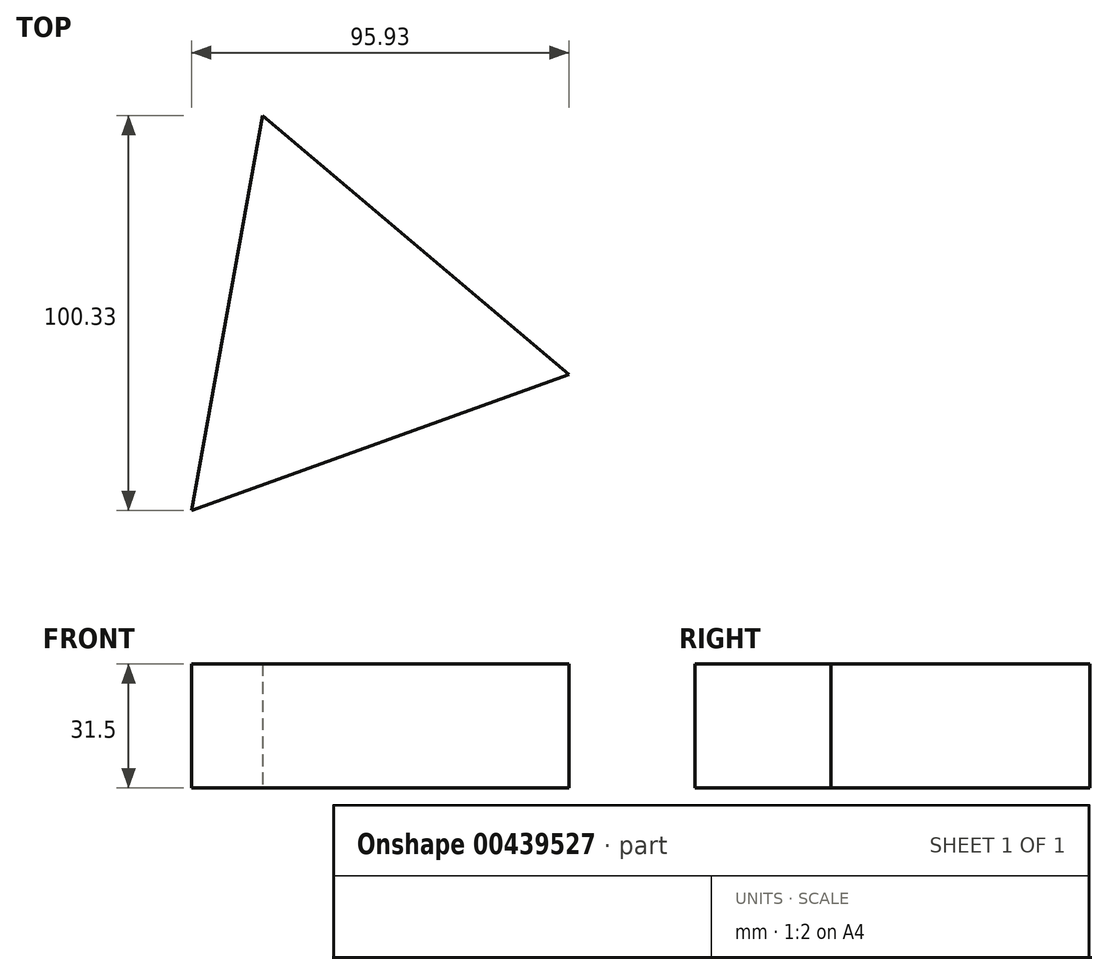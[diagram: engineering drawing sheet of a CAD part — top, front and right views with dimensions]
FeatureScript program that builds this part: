
annotation { "Feature Type Name" : "Feature", "Feature Type Description" : "" }
export const myFeature = defineFeature(function(context is Context, id is Id, definition is map)
    precondition{}
    {
        {
            var Q0;
            Q0=qCreatedBy(makeId("Top.planeOp"),FACE);
            var sketch = newSketch(context, id + "F0", { "sketchPlane" : qUnion([Q0])});
            skCircle(sketch, "E0.cCircle", {"center": v(0, 14.91) * mm, "radius": 29.43 * mm, "construction": true});
            skLineSegment(sketch, "E0.0", {"start": v(57.92, 4.46) * mm, "end": v(-38.01, -30.03) * mm});
            skLineSegment(sketch, "E0.1", {"start": v(-38.01, -30.03) * mm, "end": v(-19.91, 70.3) * mm});
            skLineSegment(sketch, "E0.2", {"start": v(-19.91, 70.3) * mm, "end": v(57.92, 4.46) * mm});
            skPoint(sketch, "E0.0.midPoint", {"position": v(9.96, -12.78) * mm});
            skSolve(sketch);
        }
        {
            var Q0;
            Q0=makeQuery(id+"F0.imprint","IMPRINT",FACE,{"disambiguationData":[TD([[makeQuery(id+"F0.imprint","IMPRINT",EDGE,{"derivedFrom":sQuery(id+"F0.wireOp",EDGE,"E0.0")}),-1.0]])]});
            extrude(context, id + "F1", {"entities" : qUnion([Q0]), "depth" : 31.5 * mm});
        }
    });
